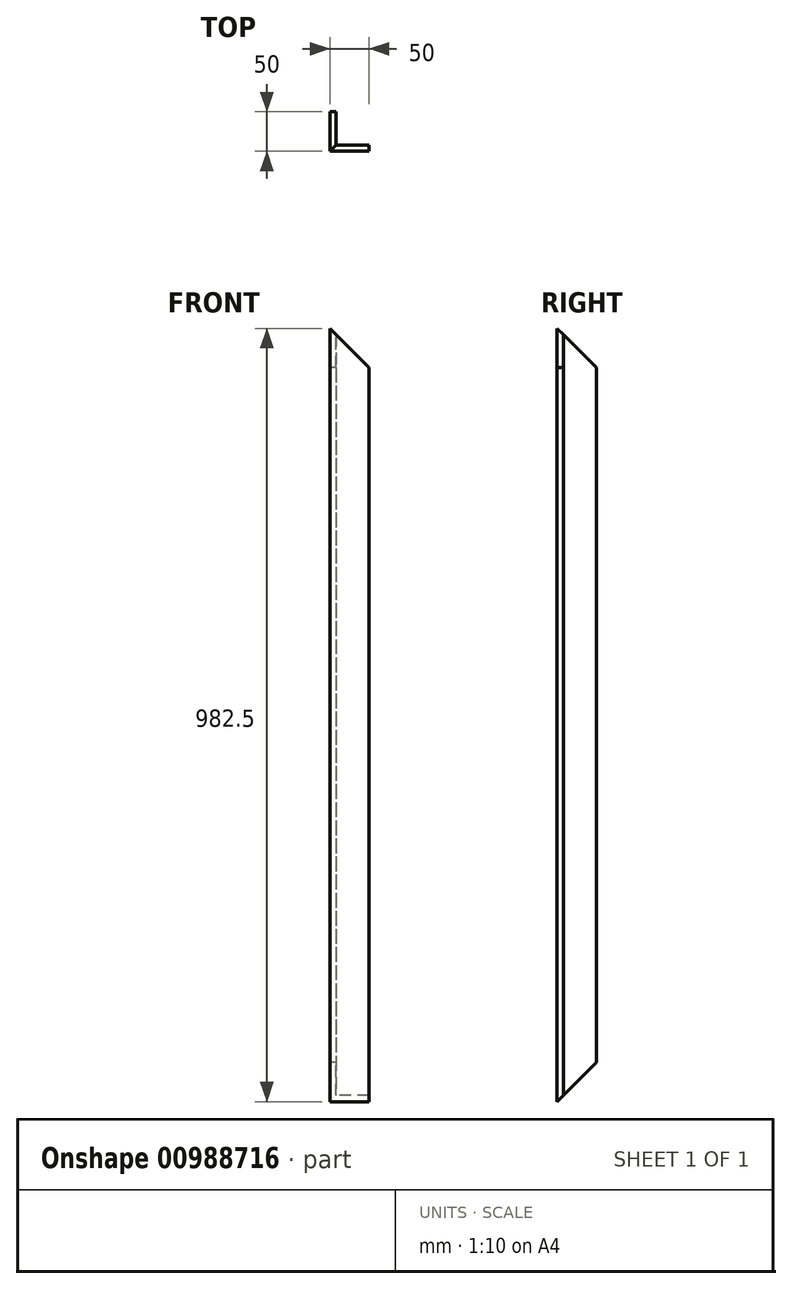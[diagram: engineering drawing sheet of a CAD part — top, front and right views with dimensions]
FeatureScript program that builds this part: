
annotation { "Feature Type Name" : "Feature", "Feature Type Description" : "" }
export const myFeature = defineFeature(function(context is Context, id is Id, definition is map)
    precondition{}
    {
        {
            var Q0;
            Q0=qCreatedBy(makeId("Top.planeOp"),FACE);
            var sketch = newSketch(context, id + "F0", { "sketchPlane" : qUnion([Q0])});
            skLineSegment(sketch, "E0", {"start": v(0, 0) * mm, "end": v(0, 50) * mm});
            skLineSegment(sketch, "E1", {"start": v(0, 50) * mm, "end": v(8, 50) * mm});
            skLineSegment(sketch, "E2", {"start": v(8, 50) * mm, "end": v(8, 8) * mm});
            skLineSegment(sketch, "E3", {"start": v(8, 8) * mm, "end": v(50, 8) * mm});
            skLineSegment(sketch, "E4", {"start": v(50, 8) * mm, "end": v(50, 0) * mm});
            skLineSegment(sketch, "E5", {"start": v(50, 0) * mm, "end": v(0, 0) * mm});
            skSolve(sketch);
        }
        {
            var Q0;
            Q0=qSketchRegion(id+"F0",true);
            extrude(context, id + "F1", {"entities" : qUnion([Q0]), "depth" : 982.5 * mm, "offsetDistance" : 25 * mm});
        }
        {
            var Q0;
            Q0=makeQuery(id+"F1.opExtrude","SWEPT_FACE",FACE,{"disambiguationData":[OSD([sQuery(id+"F0.wireOp",EDGE,"E5")])]});
            var sketch = newSketch(context, id + "F2", { "sketchPlane" : qUnion([Q0])});
            skLineSegment(sketch, "E6", {"start": v(0, 982.5) * mm, "end": v(50, 932.5) * mm});
            skLineSegment(sketch, "E7", {"start": v(50, 932.5) * mm, "end": v(50, 982.5) * mm});
            skLineSegment(sketch, "E8", {"start": v(50, 982.5) * mm, "end": v(0, 982.5) * mm});
            skSolve(sketch);
        }
        {
            var Q0;
            Q0=makeQuery(id+"F2.imprint","IMPRINT",FACE,{"disambiguationData":[TD([[makeQuery(id+"F2.imprint","IMPRINT",EDGE,{"derivedFrom":sQuery(id+"F2.wireOp",EDGE,"E6")}),1.0]])]});
            var Q1;
            Q1=makeQuery(id+"F1.opExtrude","SWEPT_FACE",FACE,{"disambiguationData":[OSD([sQuery(id+"F0.wireOp",EDGE,"E3")])]});
            extrude(context, id + "F3", {"entities" : qUnion([Q0]), "operationType" : NewBodyOperationType.REMOVE, "endBound" : BoundingType.UP_TO_SURFACE, "oppositeDirection" : true, "depth" : 25 * mm, "endBoundEntityFace" : qUnion([Q1]), "offsetDistance" : 25 * mm});
        }
        {
            var Q0;
            Q0=makeQuery(id+"F1.opExtrude","SWEPT_FACE",FACE,{"disambiguationData":[OSD([sQuery(id+"F0.wireOp",EDGE,"E0")])]});
            var sketch = newSketch(context, id + "F4", { "sketchPlane" : qUnion([Q0])});
            skLineSegment(sketch, "E9", {"start": v(0, 982.5) * mm, "end": v(0, 932.5) * mm});
            skLineSegment(sketch, "E10", {"start": v(0, 932.5) * mm, "end": v(-50, 932.5) * mm});
            skLineSegment(sketch, "E11", {"start": v(-50, 932.5) * mm, "end": v(0, 982.5) * mm});
            skSolve(sketch);
        }
        {
            var Q0;
            {var subQ0=sQuery(id+"F4.wireOp",EDGE,"E11");Q0=makeQuery(id+"F4.imprint","IMPRINT",FACE,{"disambiguationData":[TD([[makeQuery(id+"F4.imprint","IMPRINT",EDGE,{"derivedFrom":subQ0}),1.0]])]});}
            var Q1;
            Q1=makeQuery(id+"F1.opExtrude","SWEPT_FACE",FACE,{"disambiguationData":[OSD([sQuery(id+"F0.wireOp",EDGE,"E2")])]});
            extrude(context, id + "F5", {"entities" : qUnion([Q0]), "operationType" : NewBodyOperationType.REMOVE, "endBound" : BoundingType.UP_TO_SURFACE, "oppositeDirection" : true, "depth" : 25 * mm, "endBoundEntityFace" : qUnion([Q1]), "offsetDistance" : 25 * mm});
        }
        {
            var Q0;
            Q0=makeQuery(id+"F1.opExtrude","SWEPT_FACE",FACE,{"disambiguationData":[OSD([sQuery(id+"F0.wireOp",EDGE,"E0")])]});
            var sketch = newSketch(context, id + "F6", { "sketchPlane" : qUnion([Q0])});
            skLineSegment(sketch, "E12", {"start": v(0, 0) * mm, "end": v(-50, 0) * mm});
            skLineSegment(sketch, "E13", {"start": v(-50, 0) * mm, "end": v(-50, 50) * mm});
            skLineSegment(sketch, "E14", {"start": v(-50, 50) * mm, "end": v(0, 0) * mm});
            skSolve(sketch);
        }
        {
            var Q0;
            {var subQ3=sQuery(id+"F6.wireOp",EDGE,"E13");Q0=makeQuery(id+"F6.imprint","IMPRINT",FACE,{"disambiguationData":[TD([[makeQuery(id+"F6.imprint","IMPRINT",EDGE,{"derivedFrom":subQ3}),1.0]])]});}
            var Q1;
            Q1=makeQuery(id+"F1.opExtrude","SWEPT_FACE",FACE,{"disambiguationData":[OSD([sQuery(id+"F0.wireOp",EDGE,"E2")])]});
            extrude(context, id + "F7", {"entities" : qUnion([Q0]), "operationType" : NewBodyOperationType.REMOVE, "endBound" : BoundingType.THROUGH_ALL, "oppositeDirection" : true, "depth" : 25 * mm, "endBoundEntityFace" : qUnion([Q1]), "offsetDistance" : 25 * mm});
        }
    });
